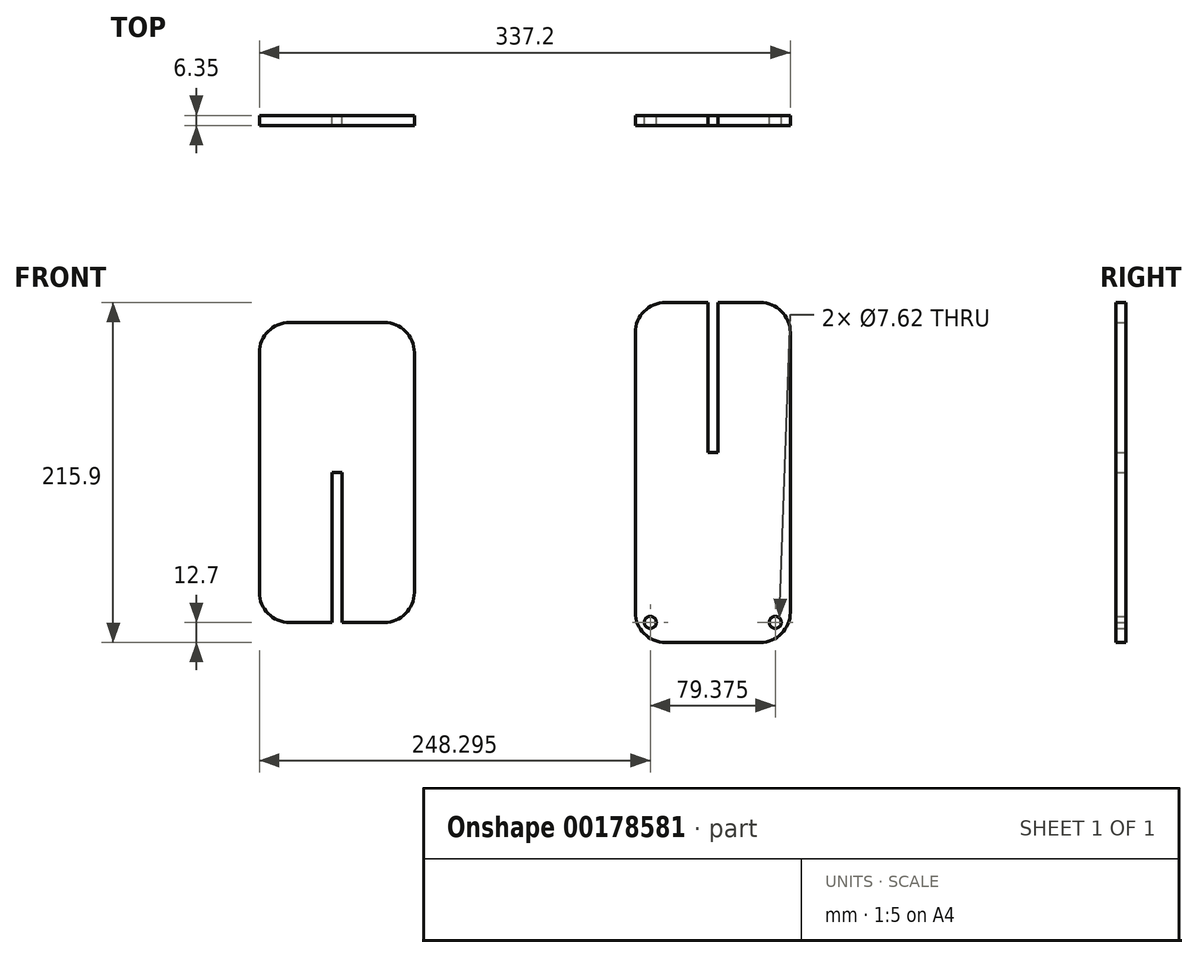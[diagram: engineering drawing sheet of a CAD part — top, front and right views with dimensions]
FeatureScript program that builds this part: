
annotation { "Feature Type Name" : "Feature", "Feature Type Description" : "" }
export const myFeature = defineFeature(function(context is Context, id is Id, definition is map)
    precondition{}
    {
        {
            var Q0;
            Q0=qCreatedBy(makeId("Front.planeOp"),FACE);
            var sketch = newSketch(context, id + "F0", { "sketchPlane" : qUnion([Q0])});
            skLineSegment(sketch, "E0.bottom", {"start": v(30.16, 95.25) * mm, "end": v(-30.16, 95.25) * mm});
            skLineSegment(sketch, "E0.top", {"start": v(30.16, -95.25) * mm, "end": v(3.17, -95.25) * mm});
            skLineSegment(sketch, "E0.left", {"start": v(49.21, 76.2) * mm, "end": v(49.21, -76.2) * mm});
            skLineSegment(sketch, "E0.right", {"start": v(-49.21, 76.2) * mm, "end": v(-49.21, -76.2) * mm});
            skPoint(sketch, "E0.middle", {"position": v(0, 0) * mm});
            skLineSegment(sketch, "E1.0", {"start": v(3.17, -95.25) * mm, "end": v(3.18, 0) * mm});
            skLineSegment(sketch, "E2.0", {"start": v(-3.18, -95.25) * mm, "end": v(-3.18, 0) * mm});
            skLineSegment(sketch, "E3", {"start": v(-3.18, 0) * mm, "end": v(3.18, 0) * mm});
            skLineSegment(sketch, "E4.trimOffspring", {"start": v(-3.18, -95.25) * mm, "end": v(-30.16, -95.25) * mm});
            skPoint(sketch, "E5.visualSharp", {"position": v(-49.21, 95.25) * mm});
            skArc(sketch, "E5.filletArc", {"start": v(-30.16, 95.25) * mm, "mid": v(-43.63, 89.67) * mm, "end": v(-49.21, 76.2) * mm});
            skPoint(sketch, "E6.visualSharp", {"position": v(49.21, 95.25) * mm});
            skArc(sketch, "E6.filletArc", {"start": v(49.21, 76.2) * mm, "mid": v(43.63, 89.67) * mm, "end": v(30.16, 95.25) * mm});
            skPoint(sketch, "E7.visualSharp", {"position": v(-49.21, -95.25) * mm});
            skArc(sketch, "E7.filletArc", {"start": v(-49.21, -76.2) * mm, "mid": v(-43.63, -89.67) * mm, "end": v(-30.16, -95.25) * mm});
            skPoint(sketch, "E8.visualSharp", {"position": v(49.21, -95.25) * mm});
            skArc(sketch, "E8.filletArc", {"start": v(30.16, -95.25) * mm, "mid": v(43.63, -89.67) * mm, "end": v(49.21, -76.2) * mm});
            skSolve(sketch);
        }
        {
            var Q0;
            Q0 = qSketchRegion(id + "F0", true);
            extrude(context, id + "F1", {"entities" : qUnion([Q0]), "depth" : 6.35 * mm, "offsetDistance" : 25.4 * mm});
        }
        {
            var Q0;
            Q0=qCreatedBy(makeId("Front.planeOp"),FACE);
            var sketch = newSketch(context, id + "F2", { "sketchPlane" : qUnion([Q0])});
            skLineSegment(sketch, "E9.bottom", {"start": v(268.94, 107.95) * mm, "end": v(241.95, 107.95) * mm});
            skLineSegment(sketch, "E9.top", {"start": v(268.94, -107.95) * mm, "end": v(208.61, -107.95) * mm});
            skLineSegment(sketch, "E9.left", {"start": v(287.99, 88.9) * mm, "end": v(287.99, -88.9) * mm});
            skLineSegment(sketch, "E9.right", {"start": v(189.56, 88.9) * mm, "end": v(189.56, -88.9) * mm});
            skPoint(sketch, "E9.middle", {"position": v(238.77, 0) * mm});
            skLineSegment(sketch, "E10", {"start": v(238.77, 107.95) * mm, "end": v(238.77, 12.7) * mm, "construction": true});
            skLineSegment(sketch, "E11.0", {"start": v(235.6, 107.95) * mm, "end": v(235.6, 12.7) * mm});
            skLineSegment(sketch, "E12.0", {"start": v(241.95, 107.95) * mm, "end": v(241.95, 12.7) * mm});
            skLineSegment(sketch, "E13", {"start": v(235.6, 12.7) * mm, "end": v(241.95, 12.7) * mm});
            skLineSegment(sketch, "E14.trimOffspring", {"start": v(235.6, 107.95) * mm, "end": v(208.61, 107.95) * mm});
            skPoint(sketch, "E15.visualSharp", {"position": v(189.56, 107.95) * mm});
            skArc(sketch, "E15.filletArc", {"start": v(208.61, 107.95) * mm, "mid": v(195.14, 102.37) * mm, "end": v(189.56, 88.9) * mm});
            skPoint(sketch, "E16.visualSharp", {"position": v(287.99, 107.95) * mm});
            skArc(sketch, "E16.filletArc", {"start": v(287.99, 88.9) * mm, "mid": v(282.4, 102.37) * mm, "end": v(268.94, 107.95) * mm});
            skPoint(sketch, "E17.visualSharp", {"position": v(189.56, -107.95) * mm});
            skArc(sketch, "E17.filletArc", {"start": v(189.56, -88.9) * mm, "mid": v(195.14, -102.37) * mm, "end": v(208.61, -107.95) * mm});
            skPoint(sketch, "E18.visualSharp", {"position": v(287.99, -107.95) * mm});
            skArc(sketch, "E18.filletArc", {"start": v(268.94, -107.95) * mm, "mid": v(282.4, -102.37) * mm, "end": v(287.99, -88.9) * mm});
            skCircle(sketch, "E19", {"center": v(199.09, -95.25) * mm, "radius": 3.81 * mm});
            skCircle(sketch, "E20", {"center": v(278.46, -95.25) * mm, "radius": 3.81 * mm});
            skSolve(sketch);
        }
        {
            var Q0;
            Q0 = qSketchRegion(id + "F2", true);
            extrude(context, id + "F3", {"entities" : qUnion([Q0]), "depth" : 6.35 * mm, "offsetDistance" : 25.4 * mm});
        }
    });
